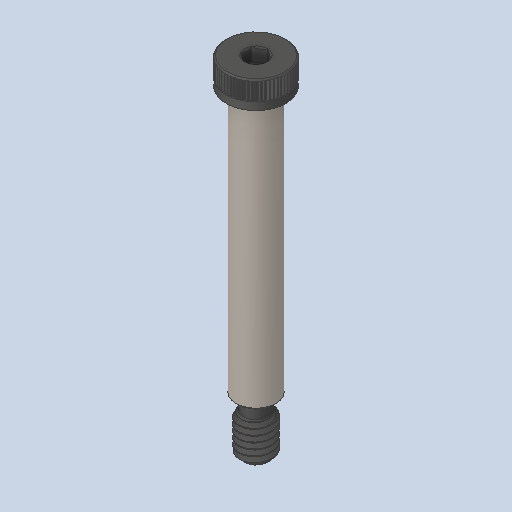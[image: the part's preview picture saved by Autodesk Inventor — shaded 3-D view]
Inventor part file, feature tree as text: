
AUTODESK INVENTOR PART (.ipt)
format: ipt  version: 2023.4 (Build 274418000, 418)  size: 426,496 bytes
history: native  units: in
note: dims shown in document units (in); Inventor stores cm internally (conversion verified against a paired STEP export)
features: chamfer x1
ambient origin geometry x8: Origin, YZ Plane, XZ Plane, XY Plane, X Axis, Y Axis, Z Axis, Center Point
bodies: Solid1 (feature_tree)
feature tree (1):
  chamfer  "Chamfer3"  [1 undecoded]
note: 1 required parameter value undecoded (feature->parameter linkage not recoverable at this tier; creation-order binding heuristic only, values carry confidence <= 0.55)
